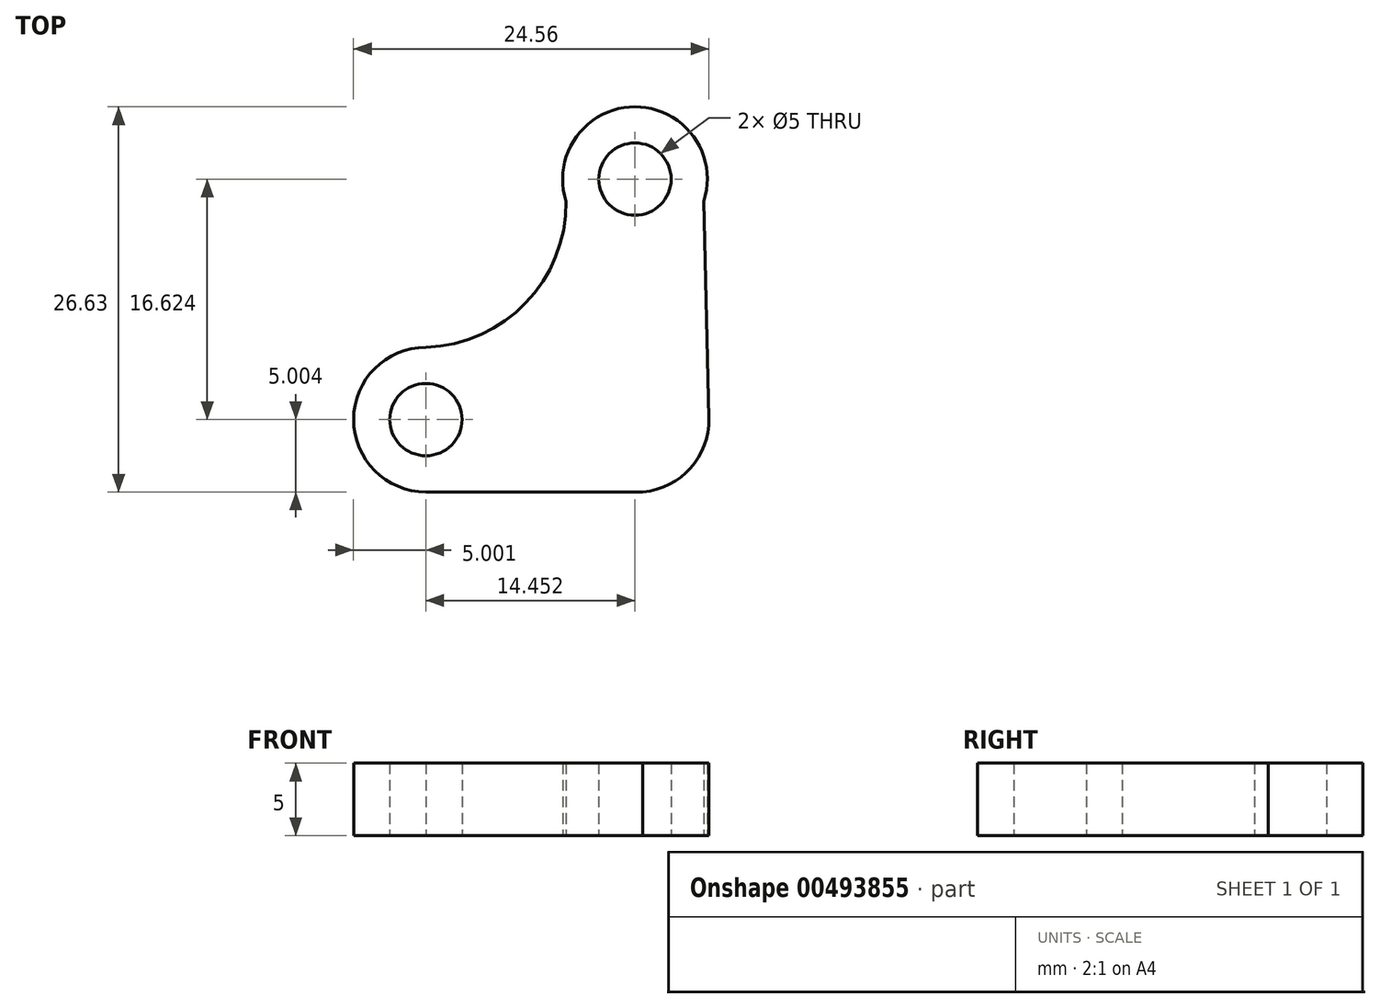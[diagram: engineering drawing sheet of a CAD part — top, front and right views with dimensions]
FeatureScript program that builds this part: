
annotation { "Feature Type Name" : "Feature", "Feature Type Description" : "" }
export const myFeature = defineFeature(function(context is Context, id is Id, definition is map)
    precondition{}
    {
        {
            var Q0;
            Q0=qCreatedBy(makeId("Top.planeOp"),FACE);
            var sketch = newSketch(context, id + "F0", { "sketchPlane" : qUnion([Q0])});
            skArc(sketch, "E0", {"start": v(-4.39, 4.9) * mm, "mid": v(-9.39, -0.1) * mm, "end": v(-4.39, -5.1) * mm});
            skArc(sketch, "E1", {"start": v(-4.39, 4.9) * mm, "mid": v(2.52, 7.97) * mm, "end": v(5.3, 15) * mm});
            skArc(sketch, "E2", {"start": v(14.82, 15) * mm, "mid": v(10.06, 21.53) * mm, "end": v(5.3, 15) * mm});
            skLineSegment(sketch, "E3", {"start": v(14.82, 15) * mm, "end": v(15.17, 0) * mm});
            skLineSegment(sketch, "E4", {"start": v(-4.39, -5.1) * mm, "end": v(10.61, -5.1) * mm});
            skCircle(sketch, "E5", {"center": v(-4.39, -0.1) * mm, "radius": 2.5 * mm});
            skCircle(sketch, "E6", {"center": v(10.06, 16.53) * mm, "radius": 2.5 * mm});
            skArc(sketch, "E7", {"start": v(10.61, -5.1) * mm, "mid": v(13.9, -3.45) * mm, "end": v(15.17, 0) * mm});
            skSolve(sketch);
        }
        {
            var Q0;
            Q0=makeQuery(id+"F0.imprint","IMPRINT",FACE,{"disambiguationData":[TD([[makeQuery(id+"F0.imprint","IMPRINT",EDGE,{"derivedFrom":sQuery(id+"F0.wireOp",EDGE,"E0")}),1.0]])]});
            extrude(context, id + "F1", {"entities" : qUnion([Q0]), "depth" : 5 * mm});
        }
    });
